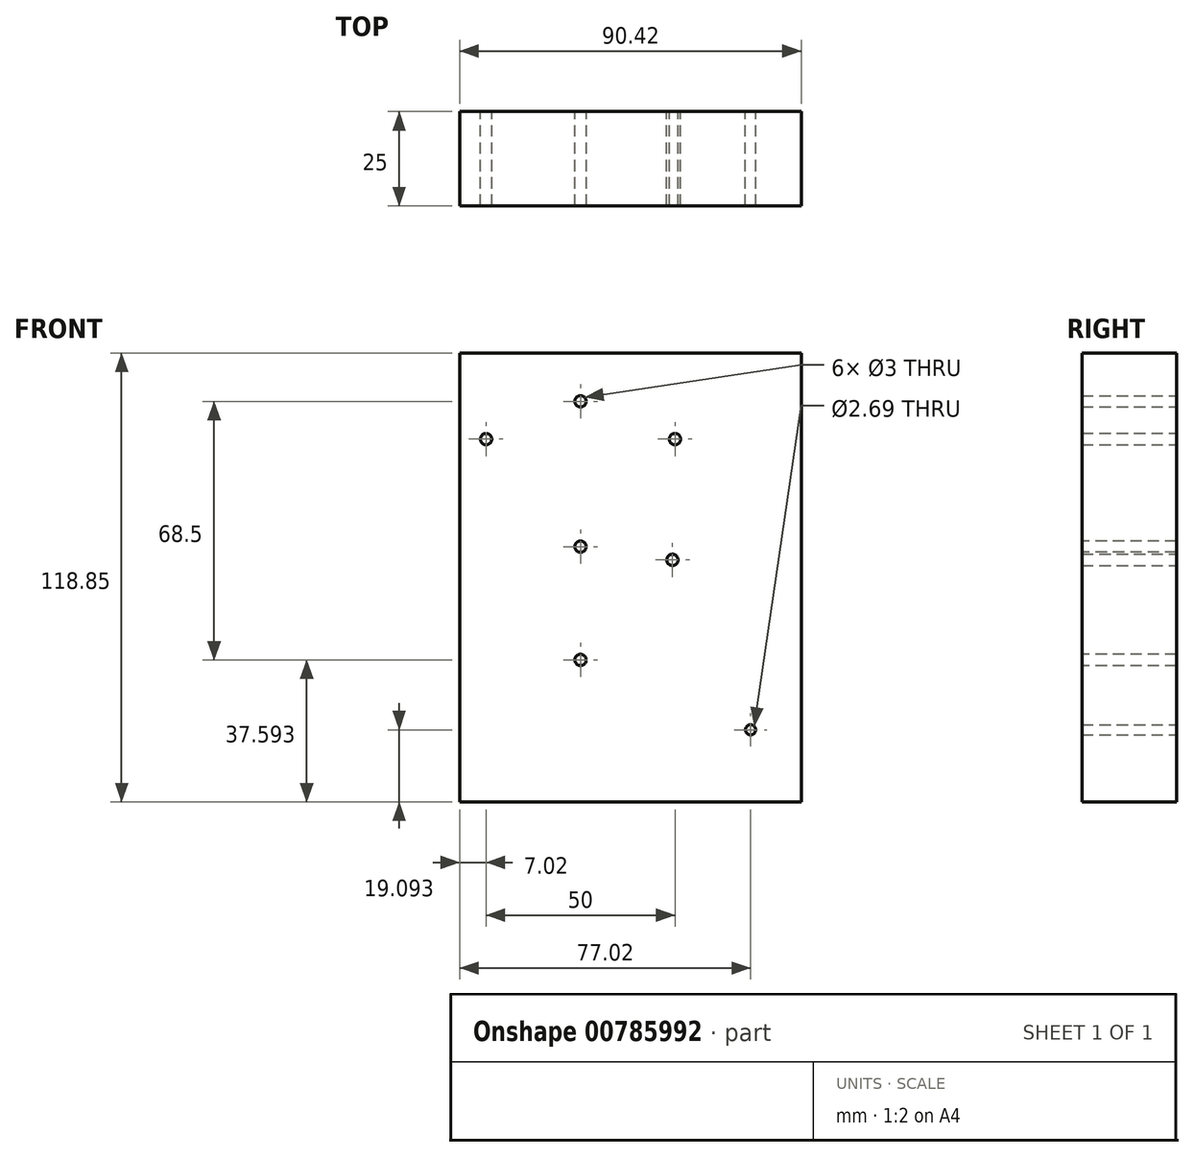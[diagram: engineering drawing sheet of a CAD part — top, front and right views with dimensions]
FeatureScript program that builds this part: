
annotation { "Feature Type Name" : "Feature", "Feature Type Description" : "" }
export const myFeature = defineFeature(function(context is Context, id is Id, definition is map)
    precondition{}
    {
        {
            var Q0;
            Q0=qCreatedBy(makeId("Front.planeOp"),FACE);
            var sketch = newSketch(context, id + "F0", { "sketchPlane" : qUnion([Q0])});
            skPoint(sketch, "E0.middle", {"position": v(0, 0) * mm});
            skCircle(sketch, "E1", {"center": v(0, -3.56) * mm, "radius": 1.5 * mm});
            skCircle(sketch, "E2", {"center": v(25, -13.56) * mm, "radius": 1.5 * mm});
            skCircle(sketch, "E3", {"center": v(-25, -13.56) * mm, "radius": 1.5 * mm});
            skCircle(sketch, "E4", {"center": v(24.31, -45.56) * mm, "radius": 1.5 * mm});
            skCircle(sketch, "E5", {"center": v(45, -90.56) * mm, "radius": 1.34 * mm});
            skLineSegment(sketch, "E6.bottom", {"start": v(-32.02, 9.2) * mm, "end": v(58.4, 9.2) * mm});
            skLineSegment(sketch, "E6.top", {"start": v(-32.02, -109.65) * mm, "end": v(58.4, -109.65) * mm});
            skLineSegment(sketch, "E6.left", {"start": v(-32.02, 9.2) * mm, "end": v(-32.02, -109.65) * mm});
            skLineSegment(sketch, "E6.right", {"start": v(58.4, 9.2) * mm, "end": v(58.4, -109.65) * mm});
            skSolve(sketch);
        }
        {
            var Q0;
            Q0=qSketchRegion(id+"F0",true);
            extrude(context, id + "F1", {"entities" : qUnion([Q0]), "depth" : 25 * mm, "offsetDistance" : 25 * mm});
        }
        {
            var Q0;
            Q0=makeQuery(id+"F1.opExtrude","CAP_FACE",FACE,{"disambiguationData":[OSD([sQuery(id+"F0.wireOp",EDGE,"E1"),sQuery(id+"F0.wireOp",EDGE,"E2"),sQuery(id+"F0.wireOp",EDGE,"E3"),sQuery(id+"F0.wireOp",EDGE,"E4"),sQuery(id+"F0.wireOp",EDGE,"E5"),sQuery(id+"F0.wireOp",EDGE,"E6.bottom"),sQuery(id+"F0.wireOp",EDGE,"E6.top"),sQuery(id+"F0.wireOp",EDGE,"E6.left"),sQuery(id+"F0.wireOp",EDGE,"E6.right")])],"isStart":false});
            var sketch = newSketch(context, id + "F2", { "sketchPlane" : qUnion([Q0])});
            skCircle(sketch, "E7", {"center": v(0, -42.06) * mm, "radius": 1.5 * mm});
            skCircle(sketch, "E8", {"center": v(0, -72.06) * mm, "radius": 1.5 * mm});
            skSolve(sketch);
        }
        {
            var Q0;
            Q0=qSketchRegion(id+"F2",true);
            extrude(context, id + "F3", {"entities" : qUnion([Q0]), "operationType" : NewBodyOperationType.REMOVE, "oppositeDirection" : true, "depth" : 25 * mm, "offsetDistance" : 25 * mm});
        }
    });
